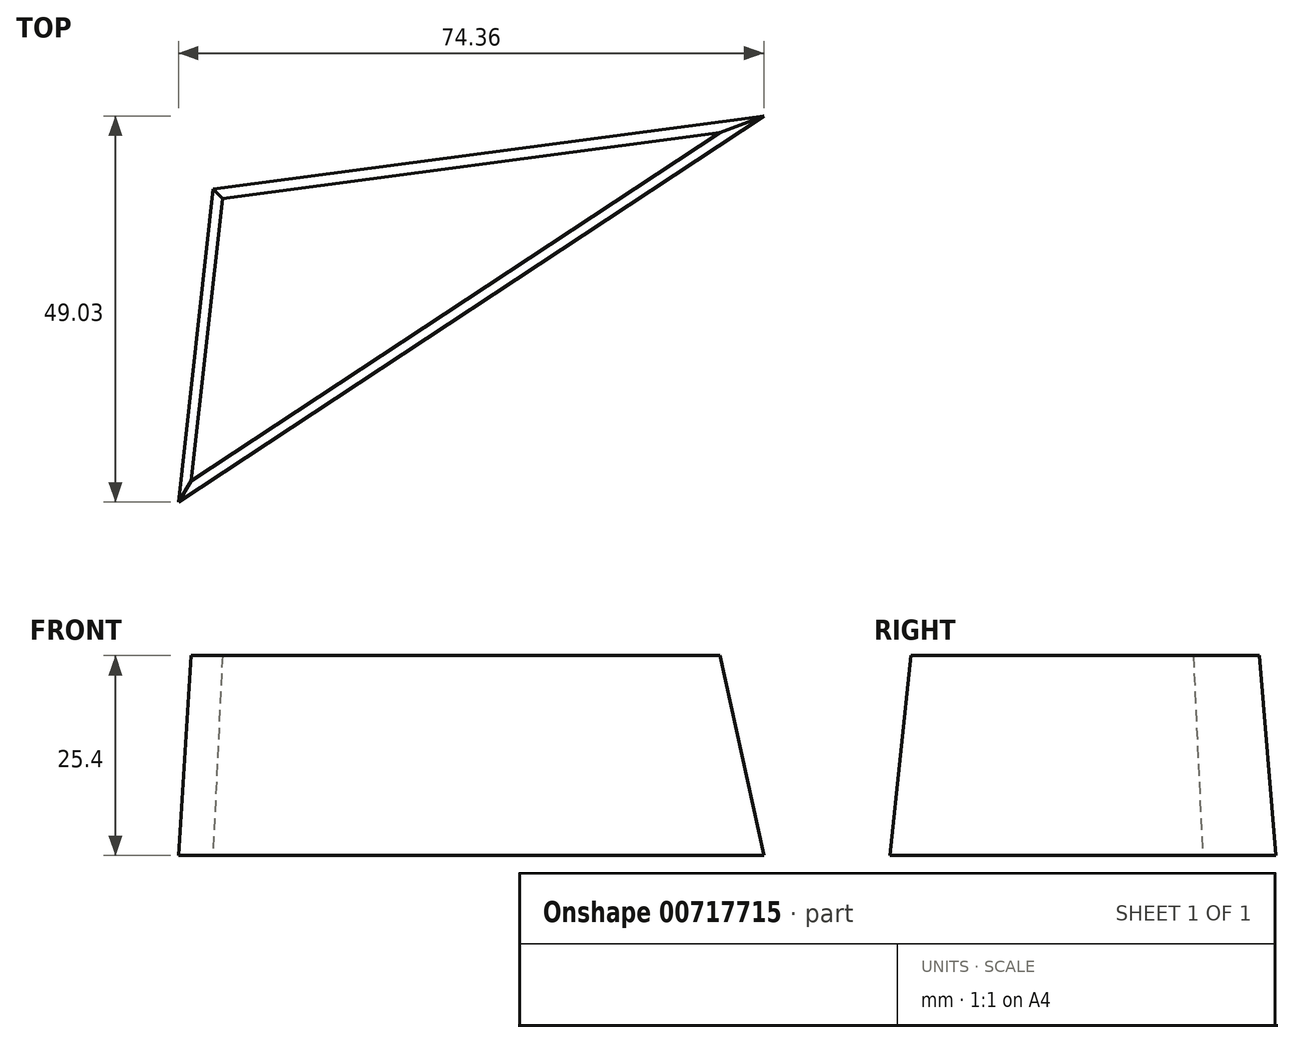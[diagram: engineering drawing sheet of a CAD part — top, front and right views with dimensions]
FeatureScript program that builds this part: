
annotation { "Feature Type Name" : "Feature", "Feature Type Description" : "" }
export const myFeature = defineFeature(function(context is Context, id is Id, definition is map)
    precondition{}
    {
        {
            var Q0;
            Q0=qCreatedBy(makeId("Top.planeOp"),FACE);
            var sketch = newSketch(context, id + "F0", { "sketchPlane" : qUnion([Q0])});
            skLineSegment(sketch, "E0", {"start": v(-48.39, -29.07) * mm, "end": v(-44.01, 10.66) * mm});
            skLineSegment(sketch, "E1", {"start": v(-44.01, 10.66) * mm, "end": v(25.97, 19.96) * mm});
            skLineSegment(sketch, "E2", {"start": v(25.97, 19.96) * mm, "end": v(-48.39, -29.07) * mm});
            skSolve(sketch);
        }
        {
            var Q0;
            Q0=makeQuery(id+"F0.imprint","IMPRINT",FACE,{"disambiguationData":[TD([[makeQuery(id+"F0.imprint","IMPRINT",EDGE,{"derivedFrom":sQuery(id+"F0.wireOp",EDGE,"E0")}),-1.0]])]});
            extrude(context, id + "F1", {"entities" : qUnion([Q0]), "depth" : 25.4 * mm, "offsetDistance" : 25.4 * mm, "hasDraft" : true, "draftAngle" : 3 * degree, "draftPullDirection" : true});
        }
    });
